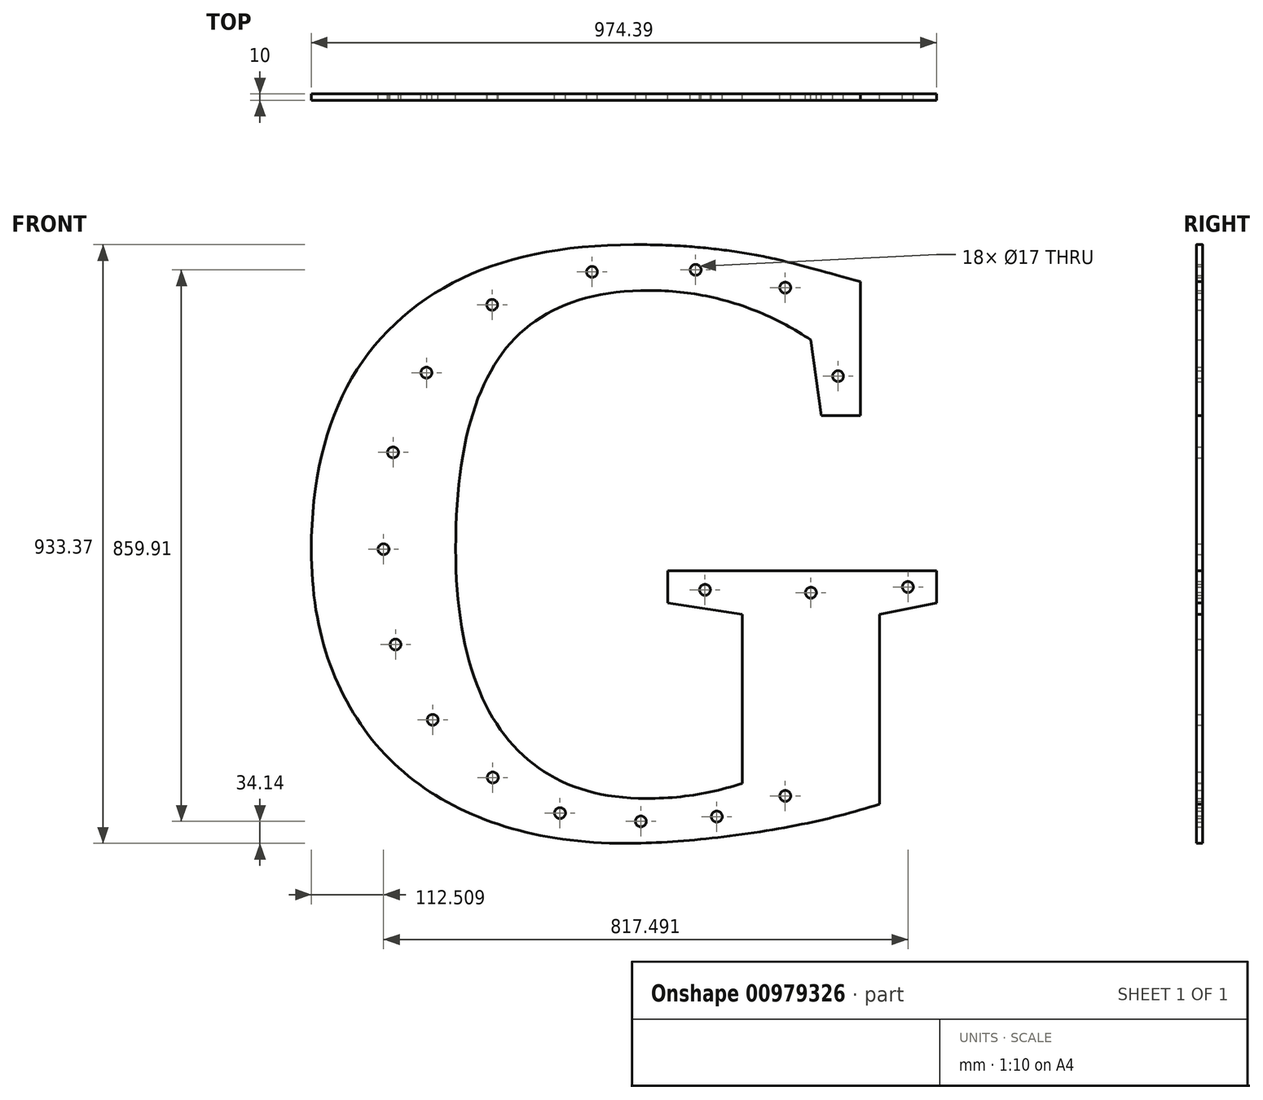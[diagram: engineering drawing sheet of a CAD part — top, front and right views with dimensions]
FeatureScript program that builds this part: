
annotation { "Feature Type Name" : "Feature", "Feature Type Description" : "" }
export const myFeature = defineFeature(function(context is Context, id is Id, definition is map)
    precondition{}
    {
        {
            var Q0;
            Q0=qCreatedBy(makeId("Front.planeOp"),FACE);
            var sketch = newSketch(context, id + "F0", { "sketchPlane" : qUnion([Q0])});
            skText(sketch, "E0", { "text": "G", "fontName": "Tinos-Bold.ttf"});
            const initialGuessF0  = {"E0": [-0.4555, -0.54873, 1, 0, 1]};
            skSetInitialGuess(sketch, initialGuessF0);
            skSolve(sketch);
        }
        {
            var Q0;
            Q0 = qSketchRegion(id + "F0", true);
            extrude(context, id + "F1", {"entities" : qUnion([Q0]), "depth" : 10 * mm, "offsetDistance" : 25 * mm});
        }
        {
            var Q0;
            Q0=makeQuery(id+"F1.opExtrude","SWEPT_FACE",FACE,{"disambiguationData":[OSD([sQuery(id+"F0.wireOp",EDGE,"E0.sketch_text.stroke-22")])]});
            var sketch = newSketch(context, id + "F2", { "sketchPlane" : qUnion([Q0])});
            skLineSegment(sketch, "E1", {"start": v(5, -137.7) * mm, "end": v(55, -137.7) * mm});
            skLineSegment(sketch, "E2", {"start": v(5, -137.7) * mm, "end": v(-45, -137.7) * mm});
            skSolve(sketch);
        }
        {
            var Q0;
            Q0=makeQuery(id+"F1.opExtrude","CAP_FACE",FACE,{"disambiguationData":[OSD([sQuery(id+"F0.wireOp",EDGE,"E0.sketch_text.stroke-0"),sQuery(id+"F0.wireOp",EDGE,"E0.sketch_text.stroke-1"),sQuery(id+"F0.wireOp",EDGE,"E0.sketch_text.stroke-2"),sQuery(id+"F0.wireOp",EDGE,"E0.sketch_text.stroke-3"),sQuery(id+"F0.wireOp",EDGE,"E0.sketch_text.stroke-4"),sQuery(id+"F0.wireOp",EDGE,"E0.sketch_text.stroke-5"),sQuery(id+"F0.wireOp",EDGE,"E0.sketch_text.stroke-6"),sQuery(id+"F0.wireOp",EDGE,"E0.sketch_text.stroke-7"),sQuery(id+"F0.wireOp",EDGE,"E0.sketch_text.stroke-8"),sQuery(id+"F0.wireOp",EDGE,"E0.sketch_text.stroke-9"),sQuery(id+"F0.wireOp",EDGE,"E0.sketch_text.stroke-10"),sQuery(id+"F0.wireOp",EDGE,"E0.sketch_text.stroke-11"),sQuery(id+"F0.wireOp",EDGE,"E0.sketch_text.stroke-12"),sQuery(id+"F0.wireOp",EDGE,"E0.sketch_text.stroke-13"),sQuery(id+"F0.wireOp",EDGE,"E0.sketch_text.stroke-14"),sQuery(id+"F0.wireOp",EDGE,"E0.sketch_text.stroke-15"),sQuery(id+"F0.wireOp",EDGE,"E0.sketch_text.stroke-16"),sQuery(id+"F0.wireOp",EDGE,"E0.sketch_text.stroke-17"),sQuery(id+"F0.wireOp",EDGE,"E0.sketch_text.stroke-18"),sQuery(id+"F0.wireOp",EDGE,"E0.sketch_text.stroke-19"),sQuery(id+"F0.wireOp",EDGE,"E0.sketch_text.stroke-20"),sQuery(id+"F0.wireOp",EDGE,"E0.sketch_text.stroke-21"),sQuery(id+"F0.wireOp",EDGE,"E0.sketch_text.stroke-22"),sQuery(id+"F0.wireOp",EDGE,"E0.sketch_text.stroke-23"),sQuery(id+"F0.wireOp",EDGE,"E0.sketch_text.stroke-24"),sQuery(id+"F0.wireOp",EDGE,"E0.sketch_text.stroke-25"),sQuery(id+"F0.wireOp",EDGE,"E0.sketch_text.stroke-26")])],"isStart":false});
            var sketch = newSketch(context, id + "F3", { "sketchPlane" : qUnion([Q0])});
            skLineSegment(sketch, "E3", {"start": v(390.85, 222.32) * mm, "end": v(468.1, 232.97) * mm});
            skLineSegment(sketch, "E4", {"start": v(284.3, -205.63) * mm, "end": v(284.3, -137.7) * mm});
            skLineSegment(sketch, "E5", {"start": v(284.3, -137.7) * mm, "end": v(498.05, -137.7) * mm});
            skLineSegment(sketch, "E6", {"start": v(498.05, -137.7) * mm, "end": v(498.05, -205.63) * mm});
            skLineSegment(sketch, "E7", {"start": v(498.05, -205.63) * mm, "end": v(498.05, -171.67) * mm});
            skLineSegment(sketch, "E8", {"start": v(498.05, -171.67) * mm, "end": v(586.8, -162.77) * mm});
            skLineSegment(sketch, "E9", {"start": v(284.3, -171.67) * mm, "end": v(167.76, -162.77) * mm});
            skLineSegment(sketch, "E10", {"start": v(284.3, -171.67) * mm, "end": v(498.05, -171.67) * mm});
            skLineSegment(sketch, "E11", {"start": v(284.3, -468.65) * mm, "end": v(498.05, -468.65) * mm});
            skLineSegment(sketch, "E12", {"start": v(391.17, -468.65) * mm, "end": v(391.17, -171.67) * mm});
            skLineSegment(sketch, "E13", {"start": v(-387.58, -104.5) * mm, "end": v(-162.54, -103.2) * mm});
            skLineSegment(sketch, "E14", {"start": v(-162.54, -103.2) * mm, "end": v(-162.54, 313.65) * mm});
            skLineSegment(sketch, "E15", {"start": v(-162.54, 313.65) * mm, "end": v(-156.68, -508.04) * mm});
            skLineSegment(sketch, "E16", {"start": v(134.55, 335.94) * mm, "end": v(134.55, 370.98) * mm});
            skLineSegment(sketch, "E17", {"start": v(139.04, -527.86) * mm, "end": v(139.29, -561.72) * mm});
            skPoint(sketch, "E18.1.internal.snap0", {"position": v(-275.06, -103.85) * mm});
            skFitSpline(sketch, "E18", {"points": [v(-275.06, -103.85) * mm, v(-275.06, -169.62) * mm, v(-238.87, -299.23) * mm, v(-157.33, -416.25) * mm, v(0, -515.24) * mm, v(139.04, -527.86) * mm, v(283.16, -513.44) * mm, v(391.17, -468.65) * mm], "startDerivative": vector(-43.8, -588.39) * mm, "endDerivative": vector(755.75, 386.52) * mm});
            skFitSpline(sketch, "E19", {"points": [v(-275.06, -103.85) * mm, v(-275.06, -35.24) * mm, v(-260.24, 47.06) * mm, v(-208.17, 171.35) * mm, v(-161.94, 230.13) * mm, v(-105.72, 277.16) * mm, v(-20.06, 314.1) * mm, v(134.55, 335.94) * mm, v(253.71, 325.87) * mm, v(371.28, 293.95) * mm, v(429.47, 227.65) * mm], "startDerivative": vector(-24.73, 825.4) * mm, "endDerivative": vector(505.6, -797.95) * mm});
            skLineSegment(sketch, "E20", {"start": v(391.17, -171.67) * mm, "end": v(391.17, -320.16) * mm});
            skCircle(sketch, "E21", {"center": v(226.02, -167.22) * mm, "radius": 8.5 * mm});
            skCircle(sketch, "E22", {"center": v(391.17, -171.67) * mm, "radius": 8.5 * mm});
            skCircle(sketch, "E23", {"center": v(542.43, -162.77) * mm, "radius": 8.5 * mm});
            skPoint(sketch, "E23.centerSnap0", {"position": v(542.43, -167.22) * mm});
            skLineSegment(sketch, "E24", {"start": v(391.17, -320.16) * mm, "end": v(391.17, -468.65) * mm});
            skCircle(sketch, "E25", {"center": v(391.17, -394.4) * mm, "radius": 8.5 * mm});
            skLineSegment(sketch, "E26", {"start": v(429.47, 227.65) * mm, "end": v(437.61, 104.27) * mm});
            skCircle(sketch, "E27", {"center": v(433.54, 165.96) * mm, "radius": 8.5 * mm});
            skCircle(sketch, "E28", {"center": v(-105.72, 277.16) * mm, "radius": 8.5 * mm});
            skCircle(sketch, "E29", {"center": v(-275.06, -103.85) * mm, "radius": 8.5 * mm});
            skCircle(sketch, "E30", {"center": v(-260.24, 47.06) * mm, "radius": 8.5 * mm});
            skCircle(sketch, "E31", {"center": v(-208.17, 171.35) * mm, "radius": 8.5 * mm});
            skCircle(sketch, "E32", {"center": v(49.96, 328.47) * mm, "radius": 8.5 * mm});
            skCircle(sketch, "E33", {"center": v(211.5, 331.65) * mm, "radius": 8.5 * mm});
            skCircle(sketch, "E34", {"center": v(351.2, 303.95) * mm, "radius": 8.5 * mm});
            skCircle(sketch, "E35", {"center": v(-256.37, -252.43) * mm, "radius": 8.5 * mm});
            skCircle(sketch, "E36", {"center": v(-198.47, -369.87) * mm, "radius": 8.5 * mm});
            skCircle(sketch, "E37", {"center": v(-104.74, -459.85) * mm, "radius": 8.5 * mm});
            skCircle(sketch, "E38", {"center": v(0, -515.24) * mm, "radius": 8.5 * mm});
            skCircle(sketch, "E39", {"center": v(126.05, -528.26) * mm, "radius": 8.5 * mm});
            skCircle(sketch, "E40", {"center": v(244.5, -520.75) * mm, "radius": 8.5 * mm});
            skCircle(sketch, "E41", {"center": v(351.2, -488.48) * mm, "radius": 8.5 * mm});
            skCircle(sketch, "E42", {"center": v(391.17, -266.84) * mm, "radius": 8.5 * mm});
            skPoint(sketch, "E43.orphan", {"position": v(407.12, 104.27) * mm});
            skPoint(sketch, "E44.end.orphan", {"position": v(-138.02, 100.38) * mm});
            skPoint(sketch, "E45.orphan", {"position": v(134.55, 102.32) * mm});
            skSolve(sketch);
        }
        {
            var Q0;
            {var subQ0=sQuery(id+"F3.wireOp",EDGE,"E21");var subQ1=sQuery(id+"F3.wireOp",EDGE,"E9");var subQ2=makeQuery(id+"F3.imprint","INTERSECT",VERTEX,{"disambiguationData":[OD(0.0)],"derivedFrom":[subQ1,subQ0]});Q0=makeQuery(id+"F3.imprint","IMPRINT",FACE,{"disambiguationData":[TD([[makeQuery(id+"F3.imprint","IMPRINT",EDGE,{"disambiguationData":[TD([[subQ2,-1.0]])],"derivedFrom":subQ1}),1.0]])]});}
            var Q1;
            {var subQ0=sQuery(id+"F3.wireOp",EDGE,"E21");var subQ1=sQuery(id+"F3.wireOp",EDGE,"E9");var subQ2=makeQuery(id+"F3.imprint","INTERSECT",VERTEX,{"disambiguationData":[OD(0.0)],"derivedFrom":[subQ1,subQ0]});Q1=makeQuery(id+"F3.imprint","IMPRINT",FACE,{"disambiguationData":[TD([[makeQuery(id+"F3.imprint","IMPRINT",EDGE,{"disambiguationData":[TD([[subQ2,-1.0]])],"derivedFrom":subQ1}),-1.0]])]});}
            var Q2;
            {var subQ0=sQuery(id+"F3.wireOp",EDGE,"E10");var subQ1=makeQuery(id+"F3.imprint","INTERSECT",VERTEX,{"derivedFrom":[subQ0,sQuery(id+"F3.wireOp",EDGE,"E20")]});Q2=makeQuery(id+"F3.imprint","IMPRINT",FACE,{"disambiguationData":[TD([[makeQuery(id+"F3.imprint","IMPRINT",EDGE,{"disambiguationData":[TD([[subQ1,1.0]])],"derivedFrom":subQ0}),1.0]])]});}
            var Q3;
            {var subQ0=sQuery(id+"F3.wireOp",EDGE,"E20");var subQ1=sQuery(id+"F3.wireOp",EDGE,"E10");var subQ2=makeQuery(id+"F3.imprint","INTERSECT",VERTEX,{"derivedFrom":[subQ1,subQ0]});Q3=makeQuery(id+"F3.imprint","IMPRINT",FACE,{"disambiguationData":[TD([[makeQuery(id+"F3.imprint","IMPRINT",EDGE,{"disambiguationData":[TD([[subQ2,-1.0]])],"derivedFrom":subQ1}),-1.0]])]});}
            var Q4;
            {var subQ0=sQuery(id+"F3.wireOp",EDGE,"E20");var subQ1=sQuery(id+"F3.wireOp",EDGE,"E10");var subQ2=makeQuery(id+"F3.imprint","INTERSECT",VERTEX,{"derivedFrom":[subQ1,subQ0]});Q4=makeQuery(id+"F3.imprint","IMPRINT",FACE,{"disambiguationData":[TD([[makeQuery(id+"F3.imprint","IMPRINT",EDGE,{"disambiguationData":[TD([[subQ2,1.0]])],"derivedFrom":subQ1}),-1.0]])]});}
            var Q5;
            {var subQ0=sQuery(id+"F3.wireOp",EDGE,"E23");var subQ1=sQuery(id+"F3.wireOp",EDGE,"E8");var subQ2=makeQuery(id+"F3.imprint","INTERSECT",VERTEX,{"disambiguationData":[OD(0.0)],"derivedFrom":[subQ1,subQ0]});Q5=makeQuery(id+"F3.imprint","IMPRINT",FACE,{"disambiguationData":[TD([[makeQuery(id+"F3.imprint","IMPRINT",EDGE,{"disambiguationData":[TD([[subQ2,-1.0]])],"derivedFrom":subQ1}),1.0]])]});}
            var Q6;
            {var subQ0=sQuery(id+"F3.wireOp",EDGE,"E23");var subQ1=sQuery(id+"F3.wireOp",EDGE,"E8");var subQ2=makeQuery(id+"F3.imprint","INTERSECT",VERTEX,{"disambiguationData":[OD(0.0)],"derivedFrom":[subQ1,subQ0]});Q6=makeQuery(id+"F3.imprint","IMPRINT",FACE,{"disambiguationData":[TD([[makeQuery(id+"F3.imprint","IMPRINT",EDGE,{"disambiguationData":[TD([[subQ2,-1.0]])],"derivedFrom":subQ1}),-1.0]])]});}
            var Q7;
            {var subQ0=sQuery(id+"F3.wireOp",EDGE,"E42");var subQ1=sQuery(id+"F3.wireOp",EDGE,"E20");var subQ2=makeQuery(id+"F3.imprint","INTERSECT",VERTEX,{"disambiguationData":[OD(0.0)],"derivedFrom":[subQ1,subQ0]});Q7=makeQuery(id+"F3.imprint","IMPRINT",FACE,{"disambiguationData":[TD([[makeQuery(id+"F3.imprint","IMPRINT",EDGE,{"disambiguationData":[TD([[subQ2,-1.0]])],"derivedFrom":subQ1}),1.0]])]});}
            var Q8;
            {var subQ0=sQuery(id+"F3.wireOp",EDGE,"E42");var subQ1=sQuery(id+"F3.wireOp",EDGE,"E20");var subQ2=makeQuery(id+"F3.imprint","INTERSECT",VERTEX,{"disambiguationData":[OD(0.0)],"derivedFrom":[subQ1,subQ0]});Q8=makeQuery(id+"F3.imprint","IMPRINT",FACE,{"disambiguationData":[TD([[makeQuery(id+"F3.imprint","IMPRINT",EDGE,{"disambiguationData":[TD([[subQ2,-1.0]])],"derivedFrom":subQ1}),-1.0]])]});}
            var Q9;
            {var subQ0=sQuery(id+"F3.wireOp",EDGE,"E25");var subQ1=sQuery(id+"F3.wireOp",EDGE,"E24");var subQ2=makeQuery(id+"F3.imprint","INTERSECT",VERTEX,{"disambiguationData":[OD(0.0)],"derivedFrom":[subQ1,subQ0]});Q9=makeQuery(id+"F3.imprint","IMPRINT",FACE,{"disambiguationData":[TD([[makeQuery(id+"F3.imprint","IMPRINT",EDGE,{"disambiguationData":[TD([[subQ2,-1.0]])],"derivedFrom":subQ1}),1.0]])]});}
            var Q10;
            {var subQ0=sQuery(id+"F3.wireOp",EDGE,"E25");var subQ1=sQuery(id+"F3.wireOp",EDGE,"E24");var subQ2=makeQuery(id+"F3.imprint","INTERSECT",VERTEX,{"disambiguationData":[OD(0.0)],"derivedFrom":[subQ1,subQ0]});Q10=makeQuery(id+"F3.imprint","IMPRINT",FACE,{"disambiguationData":[TD([[makeQuery(id+"F3.imprint","IMPRINT",EDGE,{"disambiguationData":[TD([[subQ2,-1.0]])],"derivedFrom":subQ1}),-1.0]])]});}
            var Q11;
            {var subQ0=sQuery(id+"F3.wireOp",EDGE,"E41");var subQ1=sQuery(id+"F3.wireOp",EDGE,"E18");var subQ2=makeQuery(id+"F3.imprint","INTERSECT",VERTEX,{"disambiguationData":[OD(0.0)],"derivedFrom":[subQ1,subQ0]});Q11=makeQuery(id+"F3.imprint","IMPRINT",FACE,{"disambiguationData":[TD([[makeQuery(id+"F3.imprint","IMPRINT",EDGE,{"disambiguationData":[TD([[subQ2,-1.0]])],"derivedFrom":subQ1}),-1.0]])]});}
            var Q12;
            {var subQ0=sQuery(id+"F3.wireOp",EDGE,"E41");var subQ1=sQuery(id+"F3.wireOp",EDGE,"E18");var subQ2=makeQuery(id+"F3.imprint","INTERSECT",VERTEX,{"disambiguationData":[OD(0.0)],"derivedFrom":[subQ1,subQ0]});Q12=makeQuery(id+"F3.imprint","IMPRINT",FACE,{"disambiguationData":[TD([[makeQuery(id+"F3.imprint","IMPRINT",EDGE,{"disambiguationData":[TD([[subQ2,-1.0]])],"derivedFrom":subQ1}),1.0]])]});}
            var Q13;
            {var subQ0=sQuery(id+"F3.wireOp",EDGE,"E40");var subQ1=sQuery(id+"F3.wireOp",EDGE,"E18");var subQ2=makeQuery(id+"F3.imprint","INTERSECT",VERTEX,{"disambiguationData":[OD(0.0)],"derivedFrom":[subQ1,subQ0]});Q13=makeQuery(id+"F3.imprint","IMPRINT",FACE,{"disambiguationData":[TD([[makeQuery(id+"F3.imprint","IMPRINT",EDGE,{"disambiguationData":[TD([[subQ2,-1.0]])],"derivedFrom":subQ1}),-1.0]])]});}
            var Q14;
            {var subQ0=sQuery(id+"F3.wireOp",EDGE,"E40");var subQ1=sQuery(id+"F3.wireOp",EDGE,"E18");var subQ2=makeQuery(id+"F3.imprint","INTERSECT",VERTEX,{"disambiguationData":[OD(0.0)],"derivedFrom":[subQ1,subQ0]});Q14=makeQuery(id+"F3.imprint","IMPRINT",FACE,{"disambiguationData":[TD([[makeQuery(id+"F3.imprint","IMPRINT",EDGE,{"disambiguationData":[TD([[subQ2,-1.0]])],"derivedFrom":subQ1}),1.0]])]});}
            var Q15;
            {var subQ0=sQuery(id+"F3.wireOp",EDGE,"E39");var subQ1=sQuery(id+"F3.wireOp",EDGE,"E18");var subQ2=makeQuery(id+"F3.imprint","INTERSECT",VERTEX,{"disambiguationData":[OD(0.0)],"derivedFrom":[subQ1,subQ0]});Q15=makeQuery(id+"F3.imprint","IMPRINT",FACE,{"disambiguationData":[TD([[makeQuery(id+"F3.imprint","IMPRINT",EDGE,{"disambiguationData":[TD([[subQ2,-1.0]])],"derivedFrom":subQ1}),1.0]])]});}
            var Q16;
            {var subQ0=sQuery(id+"F3.wireOp",EDGE,"E39");var subQ1=sQuery(id+"F3.wireOp",EDGE,"E18");var subQ2=makeQuery(id+"F3.imprint","INTERSECT",VERTEX,{"disambiguationData":[OD(0.0)],"derivedFrom":[subQ1,subQ0]});Q16=makeQuery(id+"F3.imprint","IMPRINT",FACE,{"disambiguationData":[TD([[makeQuery(id+"F3.imprint","IMPRINT",EDGE,{"disambiguationData":[TD([[subQ2,-1.0]])],"derivedFrom":subQ1}),-1.0]])]});}
            var Q17;
            {var subQ0=sQuery(id+"F3.wireOp",EDGE,"E38");var subQ1=sQuery(id+"F3.wireOp",EDGE,"E18");var subQ2=makeQuery(id+"F3.imprint","INTERSECT",VERTEX,{"disambiguationData":[OD(0.0)],"derivedFrom":[subQ1,subQ0]});Q17=makeQuery(id+"F3.imprint","IMPRINT",FACE,{"disambiguationData":[TD([[makeQuery(id+"F3.imprint","IMPRINT",EDGE,{"disambiguationData":[TD([[subQ2,-1.0]])],"derivedFrom":subQ1}),1.0]])]});}
            var Q18;
            {var subQ0=sQuery(id+"F3.wireOp",EDGE,"E38");var subQ1=sQuery(id+"F3.wireOp",EDGE,"E18");var subQ2=makeQuery(id+"F3.imprint","INTERSECT",VERTEX,{"disambiguationData":[OD(0.0)],"derivedFrom":[subQ1,subQ0]});Q18=makeQuery(id+"F3.imprint","IMPRINT",FACE,{"disambiguationData":[TD([[makeQuery(id+"F3.imprint","IMPRINT",EDGE,{"disambiguationData":[TD([[subQ2,-1.0]])],"derivedFrom":subQ1}),-1.0]])]});}
            var Q19;
            {var subQ0=sQuery(id+"F3.wireOp",EDGE,"E37");var subQ1=sQuery(id+"F3.wireOp",EDGE,"E18");var subQ2=makeQuery(id+"F3.imprint","INTERSECT",VERTEX,{"disambiguationData":[OD(0.0)],"derivedFrom":[subQ1,subQ0]});Q19=makeQuery(id+"F3.imprint","IMPRINT",FACE,{"disambiguationData":[TD([[makeQuery(id+"F3.imprint","IMPRINT",EDGE,{"disambiguationData":[TD([[subQ2,-1.0]])],"derivedFrom":subQ1}),1.0]])]});}
            var Q20;
            {var subQ0=sQuery(id+"F3.wireOp",EDGE,"E37");var subQ1=sQuery(id+"F3.wireOp",EDGE,"E18");var subQ2=makeQuery(id+"F3.imprint","INTERSECT",VERTEX,{"disambiguationData":[OD(0.0)],"derivedFrom":[subQ1,subQ0]});Q20=makeQuery(id+"F3.imprint","IMPRINT",FACE,{"disambiguationData":[TD([[makeQuery(id+"F3.imprint","IMPRINT",EDGE,{"disambiguationData":[TD([[subQ2,-1.0]])],"derivedFrom":subQ1}),-1.0]])]});}
            var Q21;
            {var subQ0=sQuery(id+"F3.wireOp",EDGE,"E36");var subQ1=sQuery(id+"F3.wireOp",EDGE,"E18");var subQ2=makeQuery(id+"F3.imprint","INTERSECT",VERTEX,{"disambiguationData":[OD(0.0)],"derivedFrom":[subQ1,subQ0]});Q21=makeQuery(id+"F3.imprint","IMPRINT",FACE,{"disambiguationData":[TD([[makeQuery(id+"F3.imprint","IMPRINT",EDGE,{"disambiguationData":[TD([[subQ2,-1.0]])],"derivedFrom":subQ1}),1.0]])]});}
            var Q22;
            {var subQ0=sQuery(id+"F3.wireOp",EDGE,"E36");var subQ1=sQuery(id+"F3.wireOp",EDGE,"E18");var subQ2=makeQuery(id+"F3.imprint","INTERSECT",VERTEX,{"disambiguationData":[OD(0.0)],"derivedFrom":[subQ1,subQ0]});Q22=makeQuery(id+"F3.imprint","IMPRINT",FACE,{"disambiguationData":[TD([[makeQuery(id+"F3.imprint","IMPRINT",EDGE,{"disambiguationData":[TD([[subQ2,-1.0]])],"derivedFrom":subQ1}),-1.0]])]});}
            var Q23;
            {var subQ0=sQuery(id+"F3.wireOp",EDGE,"E35");var subQ1=sQuery(id+"F3.wireOp",EDGE,"E18");var subQ2=makeQuery(id+"F3.imprint","INTERSECT",VERTEX,{"disambiguationData":[OD(0.0)],"derivedFrom":[subQ1,subQ0]});Q23=makeQuery(id+"F3.imprint","IMPRINT",FACE,{"disambiguationData":[TD([[makeQuery(id+"F3.imprint","IMPRINT",EDGE,{"disambiguationData":[TD([[subQ2,-1.0]])],"derivedFrom":subQ1}),1.0]])]});}
            var Q24;
            {var subQ0=sQuery(id+"F3.wireOp",EDGE,"E35");var subQ1=sQuery(id+"F3.wireOp",EDGE,"E18");var subQ2=makeQuery(id+"F3.imprint","INTERSECT",VERTEX,{"disambiguationData":[OD(0.0)],"derivedFrom":[subQ1,subQ0]});Q24=makeQuery(id+"F3.imprint","IMPRINT",FACE,{"disambiguationData":[TD([[makeQuery(id+"F3.imprint","IMPRINT",EDGE,{"disambiguationData":[TD([[subQ2,-1.0]])],"derivedFrom":subQ1}),-1.0]])]});}
            var Q25;
            {var subQ1=sQuery(id+"F3.wireOp",EDGE,"E13");var subQ3=sQuery(id+"F3.wireOp",EDGE,"E29");var subQ4=makeQuery(id+"F3.imprint","INTERSECT",VERTEX,{"disambiguationData":[OD(1.0)],"derivedFrom":[subQ1,subQ3]});Q25=makeQuery(id+"F3.imprint","IMPRINT",FACE,{"disambiguationData":[TD([[makeQuery(id+"F3.imprint","IMPRINT",EDGE,{"disambiguationData":[TD([[subQ4,1.0]])],"derivedFrom":subQ3}),1.0]])]});}
            var Q26;
            {var subQ1=sQuery(id+"F3.wireOp",EDGE,"E13");var subQ3=sQuery(id+"F3.wireOp",EDGE,"E29");var subQ4=makeQuery(id+"F3.imprint","INTERSECT",VERTEX,{"disambiguationData":[OD(0.0)],"derivedFrom":[subQ1,subQ3]});Q26=makeQuery(id+"F3.imprint","IMPRINT",FACE,{"disambiguationData":[TD([[makeQuery(id+"F3.imprint","IMPRINT",EDGE,{"disambiguationData":[TD([[subQ4,-1.0]])],"derivedFrom":subQ3}),1.0]])]});}
            var Q27;
            {var subQ1=sQuery(id+"F3.wireOp",EDGE,"E13");var subQ3=sQuery(id+"F3.wireOp",EDGE,"E29");var subQ4=makeQuery(id+"F3.imprint","INTERSECT",VERTEX,{"disambiguationData":[OD(0.0)],"derivedFrom":[subQ1,subQ3]});Q27=makeQuery(id+"F3.imprint","IMPRINT",FACE,{"disambiguationData":[TD([[makeQuery(id+"F3.imprint","IMPRINT",EDGE,{"disambiguationData":[TD([[subQ4,1.0]])],"derivedFrom":subQ3}),1.0]])]});}
            var Q28;
            {var subQ1=sQuery(id+"F3.wireOp",EDGE,"E13");var subQ3=sQuery(id+"F3.wireOp",EDGE,"E29");var subQ4=makeQuery(id+"F3.imprint","INTERSECT",VERTEX,{"disambiguationData":[OD(1.0)],"derivedFrom":[subQ1,subQ3]});Q28=makeQuery(id+"F3.imprint","IMPRINT",FACE,{"disambiguationData":[TD([[makeQuery(id+"F3.imprint","IMPRINT",EDGE,{"disambiguationData":[TD([[subQ4,-1.0]])],"derivedFrom":subQ3}),1.0]])]});}
            var Q29;
            {var subQ0=sQuery(id+"F3.wireOp",EDGE,"E30");var subQ1=sQuery(id+"F3.wireOp",EDGE,"E19");var subQ2=makeQuery(id+"F3.imprint","INTERSECT",VERTEX,{"disambiguationData":[OD(0.0)],"derivedFrom":[subQ1,subQ0]});Q29=makeQuery(id+"F3.imprint","IMPRINT",FACE,{"disambiguationData":[TD([[makeQuery(id+"F3.imprint","IMPRINT",EDGE,{"disambiguationData":[TD([[subQ2,-1.0]])],"derivedFrom":subQ1}),-1.0]])]});}
            var Q30;
            {var subQ0=sQuery(id+"F3.wireOp",EDGE,"E30");var subQ1=sQuery(id+"F3.wireOp",EDGE,"E19");var subQ2=makeQuery(id+"F3.imprint","INTERSECT",VERTEX,{"disambiguationData":[OD(0.0)],"derivedFrom":[subQ1,subQ0]});Q30=makeQuery(id+"F3.imprint","IMPRINT",FACE,{"disambiguationData":[TD([[makeQuery(id+"F3.imprint","IMPRINT",EDGE,{"disambiguationData":[TD([[subQ2,-1.0]])],"derivedFrom":subQ1}),1.0]])]});}
            var Q31;
            {var subQ0=sQuery(id+"F3.wireOp",EDGE,"E31");var subQ1=sQuery(id+"F3.wireOp",EDGE,"E19");var subQ2=makeQuery(id+"F3.imprint","INTERSECT",VERTEX,{"disambiguationData":[OD(0.0)],"derivedFrom":[subQ1,subQ0]});Q31=makeQuery(id+"F3.imprint","IMPRINT",FACE,{"disambiguationData":[TD([[makeQuery(id+"F3.imprint","IMPRINT",EDGE,{"disambiguationData":[TD([[subQ2,-1.0]])],"derivedFrom":subQ1}),-1.0]])]});}
            var Q32;
            {var subQ0=sQuery(id+"F3.wireOp",EDGE,"E31");var subQ1=sQuery(id+"F3.wireOp",EDGE,"E19");var subQ2=makeQuery(id+"F3.imprint","INTERSECT",VERTEX,{"disambiguationData":[OD(0.0)],"derivedFrom":[subQ1,subQ0]});Q32=makeQuery(id+"F3.imprint","IMPRINT",FACE,{"disambiguationData":[TD([[makeQuery(id+"F3.imprint","IMPRINT",EDGE,{"disambiguationData":[TD([[subQ2,-1.0]])],"derivedFrom":subQ1}),1.0]])]});}
            var Q33;
            {var subQ0=sQuery(id+"F3.wireOp",EDGE,"E28");var subQ1=sQuery(id+"F3.wireOp",EDGE,"E19");var subQ2=makeQuery(id+"F3.imprint","INTERSECT",VERTEX,{"disambiguationData":[OD(0.0)],"derivedFrom":[subQ1,subQ0]});Q33=makeQuery(id+"F3.imprint","IMPRINT",FACE,{"disambiguationData":[TD([[makeQuery(id+"F3.imprint","IMPRINT",EDGE,{"disambiguationData":[TD([[subQ2,-1.0]])],"derivedFrom":subQ1}),1.0]])]});}
            var Q34;
            {var subQ0=sQuery(id+"F3.wireOp",EDGE,"E28");var subQ1=sQuery(id+"F3.wireOp",EDGE,"E19");var subQ2=makeQuery(id+"F3.imprint","INTERSECT",VERTEX,{"disambiguationData":[OD(0.0)],"derivedFrom":[subQ1,subQ0]});Q34=makeQuery(id+"F3.imprint","IMPRINT",FACE,{"disambiguationData":[TD([[makeQuery(id+"F3.imprint","IMPRINT",EDGE,{"disambiguationData":[TD([[subQ2,-1.0]])],"derivedFrom":subQ1}),-1.0]])]});}
            var Q35;
            {var subQ0=sQuery(id+"F3.wireOp",EDGE,"E32");var subQ1=sQuery(id+"F3.wireOp",EDGE,"E19");var subQ2=makeQuery(id+"F3.imprint","INTERSECT",VERTEX,{"disambiguationData":[OD(0.0)],"derivedFrom":[subQ1,subQ0]});Q35=makeQuery(id+"F3.imprint","IMPRINT",FACE,{"disambiguationData":[TD([[makeQuery(id+"F3.imprint","IMPRINT",EDGE,{"disambiguationData":[TD([[subQ2,-1.0]])],"derivedFrom":subQ1}),1.0]])]});}
            var Q36;
            {var subQ0=sQuery(id+"F3.wireOp",EDGE,"E32");var subQ1=sQuery(id+"F3.wireOp",EDGE,"E19");var subQ2=makeQuery(id+"F3.imprint","INTERSECT",VERTEX,{"disambiguationData":[OD(0.0)],"derivedFrom":[subQ1,subQ0]});Q36=makeQuery(id+"F3.imprint","IMPRINT",FACE,{"disambiguationData":[TD([[makeQuery(id+"F3.imprint","IMPRINT",EDGE,{"disambiguationData":[TD([[subQ2,-1.0]])],"derivedFrom":subQ1}),-1.0]])]});}
            var Q37;
            {var subQ0=sQuery(id+"F3.wireOp",EDGE,"E33");var subQ1=sQuery(id+"F3.wireOp",EDGE,"E19");var subQ2=makeQuery(id+"F3.imprint","INTERSECT",VERTEX,{"disambiguationData":[OD(0.0)],"derivedFrom":[subQ1,subQ0]});Q37=makeQuery(id+"F3.imprint","IMPRINT",FACE,{"disambiguationData":[TD([[makeQuery(id+"F3.imprint","IMPRINT",EDGE,{"disambiguationData":[TD([[subQ2,-1.0]])],"derivedFrom":subQ1}),1.0]])]});}
            var Q38;
            {var subQ0=sQuery(id+"F3.wireOp",EDGE,"E33");var subQ1=sQuery(id+"F3.wireOp",EDGE,"E19");var subQ2=makeQuery(id+"F3.imprint","INTERSECT",VERTEX,{"disambiguationData":[OD(0.0)],"derivedFrom":[subQ1,subQ0]});Q38=makeQuery(id+"F3.imprint","IMPRINT",FACE,{"disambiguationData":[TD([[makeQuery(id+"F3.imprint","IMPRINT",EDGE,{"disambiguationData":[TD([[subQ2,-1.0]])],"derivedFrom":subQ1}),-1.0]])]});}
            var Q39;
            {var subQ0=sQuery(id+"F3.wireOp",EDGE,"E34");var subQ1=sQuery(id+"F3.wireOp",EDGE,"E19");var subQ2=makeQuery(id+"F3.imprint","INTERSECT",VERTEX,{"disambiguationData":[OD(0.0)],"derivedFrom":[subQ1,subQ0]});Q39=makeQuery(id+"F3.imprint","IMPRINT",FACE,{"disambiguationData":[TD([[makeQuery(id+"F3.imprint","IMPRINT",EDGE,{"disambiguationData":[TD([[subQ2,-1.0]])],"derivedFrom":subQ1}),1.0]])]});}
            var Q40;
            {var subQ0=sQuery(id+"F3.wireOp",EDGE,"E34");var subQ1=sQuery(id+"F3.wireOp",EDGE,"E19");var subQ2=makeQuery(id+"F3.imprint","INTERSECT",VERTEX,{"disambiguationData":[OD(0.0)],"derivedFrom":[subQ1,subQ0]});Q40=makeQuery(id+"F3.imprint","IMPRINT",FACE,{"disambiguationData":[TD([[makeQuery(id+"F3.imprint","IMPRINT",EDGE,{"disambiguationData":[TD([[subQ2,-1.0]])],"derivedFrom":subQ1}),-1.0]])]});}
            var Q41;
            {var subQ0=sQuery(id+"F3.wireOp",EDGE,"E27");var subQ1=sQuery(id+"F3.wireOp",EDGE,"E26");var subQ2=makeQuery(id+"F3.imprint","INTERSECT",VERTEX,{"disambiguationData":[OD(0.0)],"derivedFrom":[subQ1,subQ0]});Q41=makeQuery(id+"F3.imprint","IMPRINT",FACE,{"disambiguationData":[TD([[makeQuery(id+"F3.imprint","IMPRINT",EDGE,{"disambiguationData":[TD([[subQ2,-1.0]])],"derivedFrom":subQ1}),1.0]])]});}
            var Q42;
            {var subQ0=sQuery(id+"F3.wireOp",EDGE,"E27");var subQ1=sQuery(id+"F3.wireOp",EDGE,"E26");var subQ2=makeQuery(id+"F3.imprint","INTERSECT",VERTEX,{"disambiguationData":[OD(0.0)],"derivedFrom":[subQ1,subQ0]});Q42=makeQuery(id+"F3.imprint","IMPRINT",FACE,{"disambiguationData":[TD([[makeQuery(id+"F3.imprint","IMPRINT",EDGE,{"disambiguationData":[TD([[subQ2,-1.0]])],"derivedFrom":subQ1}),-1.0]])]});}
            extrude(context, id + "F4", {"entities" : qUnion([Q0, Q1, Q2, Q3, Q4, Q5, Q6, Q7, Q8, Q9, Q10, Q11, Q12, Q13, Q14, Q15, Q16, Q17, Q18, Q19, Q20, Q21, Q22, Q23, Q24, Q25, Q26, Q27, Q28, Q29, Q30, Q31, Q32, Q33, Q34, Q35, Q36, Q37, Q38, Q39, Q40, Q41, Q42]), "operationType" : NewBodyOperationType.REMOVE, "endBound" : BoundingType.SYMMETRIC, "depth" : 25 * mm, "offsetDistance" : 25 * mm});
        }
    });
